# Revit family: P200921MX-069c_MVWB965H_CW
name_source: partatom
category: Specialty Equipment
units: mm (PartAtom-declared; Revit-internal decimal feet)

## family parameters
Always vertical = No
Cut with Voids When Loaded = No
Enable Cutting in Views = No
Maintain Annotation Orientation = No
Part Type = Normal
Room Calculation Point = No
Round Connector Dimension = Use Diameter
Shared = No
Work Plane-Based = No

## types (2) — shared parameters
Accent Material = ARCAT - Plastic - Gray
Amps = 0 A
Back Panel Material = ARCAT - Metal - Aluminum
Clearance Material = ARCAT - Clearance
Default Elevation = 0"
Depth = 30"
Description = Top Load Large Capacity Agitator Washer – 6.0 cu. ft.
Top Load Large Capacity Agitator Washer – 6.0 cu. ft.
Dimension Guide = http://access.whirlpool.com Guide&sku=MVWB965HW&language=EN
http://access.whirlpool.com Guide&sku=MVWB965HW&language=EN
Door Material = ARCAT - Metal - Steel - Stainless
Energy Guide = https://www.whirlpool.com
https://www.whirlpool.com
Family Name = Laundry
Feature 1 = Largest Capacity Agitator Washer Available at 6.0 cu. ft.
Largest Capacity Agitator Washer Available at 6.0 cu. ft.
Feature 2 = The Most Powerful Cleaning in its class driven by the PowerWash® system
The Most Powerful Cleaning in its class driven by the PowerWash® system
Feature 3 = PowerSpray
Pulvérisation PowerSpray
Glass Material = ARCAT - Glass - Tempered - Black
Handle Material = ARCAT - Metal - Steel - Stainless
Height = 43 7/16"
Installation-Fabrication = http://access.whirlpool.com Instruction&sku=MVWB965HW&language=EN
http://access.whirlpool.com Instruction&sku=MVWB965HW&language=EN
Knob Material = ARCAT - Metal - Steel - Stainless
Leg Material = ARCAT - Plastic - White
Manufacturer = Maytag
Voltage = 0 V
Width = 29 1/2"

## per-type parameters (varying)
| type | Body Material |
| MVWB965HW | ARCAT - Metal - White |
| MVWB965HC | ARCAT - Metal - Gray |

note: column(s) folded — value = type name in every type: Model

## geometry (parser evidence)
native form markers: Sweep x6
no freeform markers — native parametric forms only
